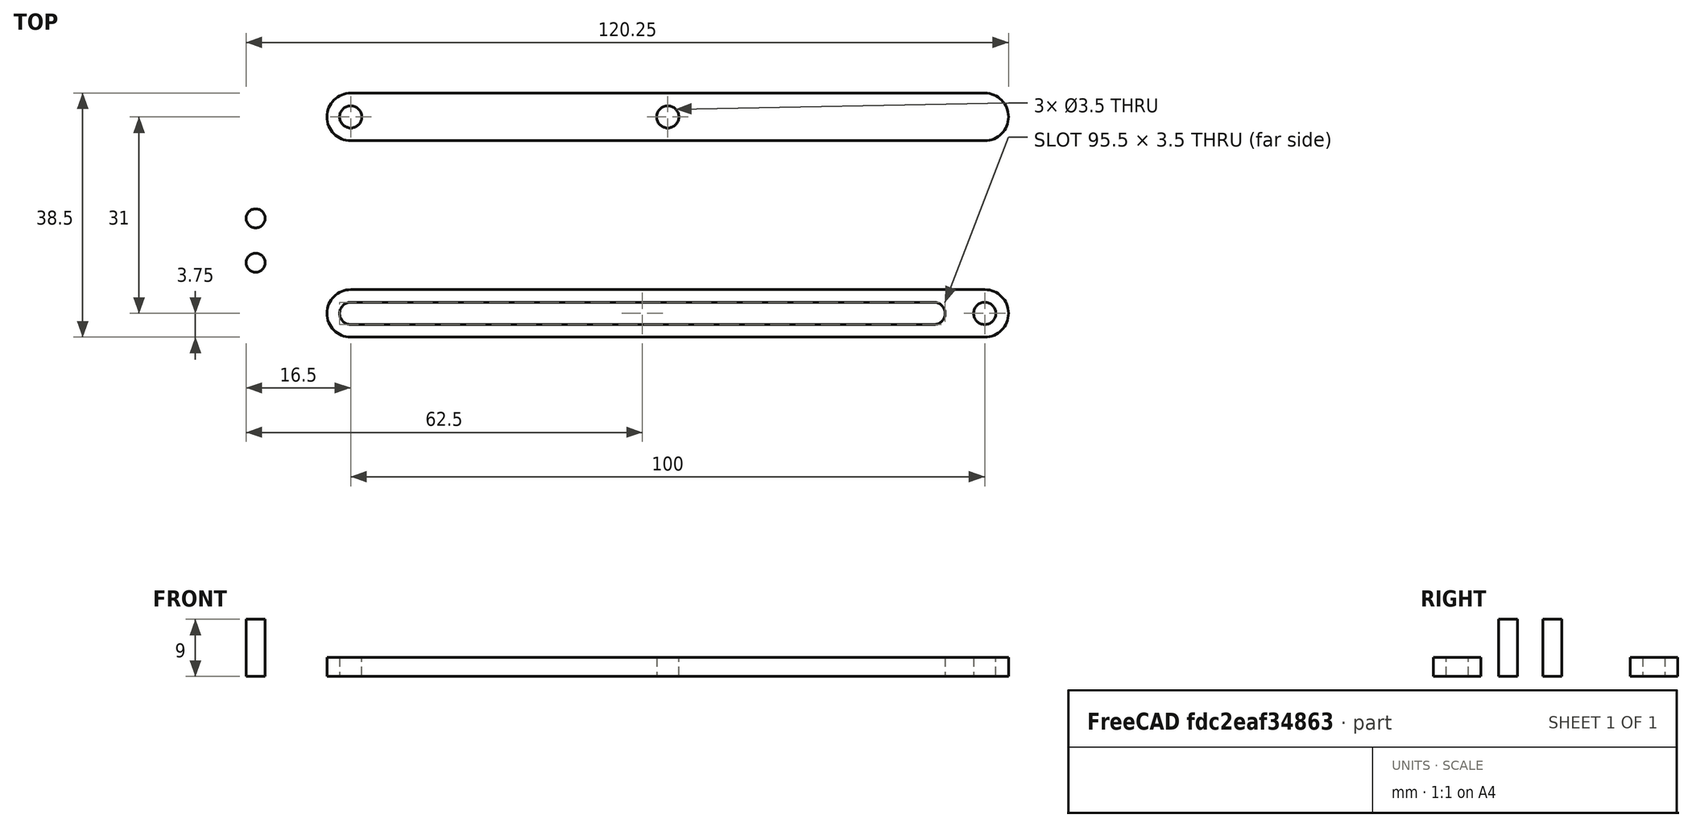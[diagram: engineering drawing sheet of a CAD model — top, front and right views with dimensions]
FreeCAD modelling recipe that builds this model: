
FCSTD DOCUMENT  (FreeCAD 1.0R39285 (Git))
Label: sissor_lift
License: All rights reserved
LicenseURL: https://en.wikipedia.org/wiki/All_rights_reserved
objects: PartDesign::Body×6, Sketcher::SketchObject×3, PartDesign::Pad×3, PartDesign::FeatureBase×3, PartDesign::SubShapeBinder×1, Assembly::JointGroup×1, Assembly::AssemblyObject×1
note: 28 computed .brp shape members not serialized (recipe doc carries the construction recipe); baked Part::Feature solids carry a one-line shape summary decoded from their .brp

FEATURE [Sketcher::SketchObject] Sketch
  ArcFitTolerance = 1e-06
  AttachmentSupport = -> [XY_Plane]
  FullyConstrained = true
  MakeInternals = false
  MapMode = 5
  sketch-geometry (9):
    g0: ArcOfCircle CenterX=-50 CenterY=2e-16 CenterZ=0 NormalX=0 NormalY=0 NormalZ=1 AngleXU=0 Radius=3.75 StartAngle=1.5708 EndAngle=4.71239
    g1: ArcOfCircle CenterX=50 CenterY=-2e-16 CenterZ=0 NormalX=0 NormalY=0 NormalZ=1 AngleXU=0 Radius=3.75 StartAngle=4.71239 EndAngle=7.85398
    g2: LineSegment StartX=-50 StartY=3.75 StartZ=0 EndX=50 EndY=3.75 EndZ=0
    g3: LineSegment StartX=-50 StartY=-3.75 StartZ=0 EndX=50 EndY=-3.75 EndZ=0
    g4: ArcOfCircle CenterX=-50 CenterY=2e-16 CenterZ=0 NormalX=0 NormalY=0 NormalZ=1 AngleXU=0 Radius=1.75 StartAngle=1.5708 EndAngle=4.71239
    g5: ArcOfCircle CenterX=42 CenterY=3e-16 CenterZ=0 NormalX=0 NormalY=0 NormalZ=1 AngleXU=0 Radius=1.75 StartAngle=4.71239 EndAngle=7.85398
    g6: LineSegment StartX=-50 StartY=1.75 StartZ=0 EndX=42 EndY=1.75 EndZ=0
    g7: LineSegment StartX=-50 StartY=-1.75 StartZ=0 EndX=42 EndY=-1.75 EndZ=0
    g8: Circle CenterX=50 CenterY=-2e-16 CenterZ=0 NormalX=0 NormalY=0 NormalZ=1 AngleXU=0 Radius=1.75
  constraints (20):
    c: Tangent(g0,g2) = 1.5708
    c: Tangent(g0,g3) = -1.5708
    c: Tangent(g1,g2) = 1.5708
    c: Tangent(g1,g3) = -1.5708
    c: Equal(g0,g1)
    c: Horizontal(g3)
    c: Symmetric(g0,g1,g-1)
    c: DistanceX(g0,g1) = 100
    c: DistanceY(g0,g0) = 7.5
    c: Tangent(g4,g6) = 1.5708
    c: Tangent(g4,g7) = -1.5708
    c: Tangent(g5,g6) = 1.5708
    c: Tangent(g5,g7) = -1.5708
    c: Equal(g4,g5)
    c: Horizontal(g7)
    c: Distance(g4,g4) = 3.5
    c: Coincident(g8,g1)
    c: Diameter(g8) = 3.5
    c: DistanceX(g5,g1) = 8
    c: Coincident(g4,g0)
FEATURE [PartDesign::Pad] Pad
  Direction = (0,0,1)
  Length = 3
  Length2 = 10
  Profile = -> Sketch
  ReferenceAxis = -> Sketch [N_Axis]
  Refine = true
  Suppressed = false
  Type = 0
FEATURE [PartDesign::Body] Body  label="base"
  AllowCompound = false
  Group = -> [Sketch,Pad]
  Origin = -> Origin
  Tip = -> Pad
FEATURE [PartDesign::SubShapeBinder] Binder
  BindCopyOnChange = 0
  BindMode = 0
  ClaimChildren = false
  Context = -> Body001 [Binder.]
  Fuse = false
  MakeFace = true
  OffsetFill = false
  OffsetIntersection = false
  OffsetJoinType = 0
  OffsetOpenResult = false
  PartialLoad = false
  Refine = true
  Relative = true
  Support = -> [Body]
  _Version = 2
FEATURE [Sketcher::SketchObject] Sketch001
  ArcFitTolerance = 1e-06
  AttachmentSupport = -> [XY_Plane001]
  ExternalGeometry = -> [Binder]
  FullyConstrained = true
  MakeInternals = false
  MapMode = 5
  sketch-geometry (6):
    g0: ArcOfCircle CenterX=-50 CenterY=1e-16 CenterZ=0 NormalX=0 NormalY=0 NormalZ=1 AngleXU=0 Radius=3.75 StartAngle=1.5708 EndAngle=4.71239
    g1: ArcOfCircle CenterX=50 CenterY=-1e-16 CenterZ=0 NormalX=0 NormalY=0 NormalZ=1 AngleXU=0 Radius=3.75 StartAngle=4.71239 EndAngle=7.85398
    g2: LineSegment StartX=-50 StartY=3.75 StartZ=0 EndX=50 EndY=3.75 EndZ=0
    g3: LineSegment StartX=-50 StartY=-3.75 StartZ=0 EndX=50 EndY=-3.75 EndZ=0
    g4: Circle CenterX=-50 CenterY=1e-16 CenterZ=0 NormalX=0 NormalY=0 NormalZ=1 AngleXU=0 Radius=1.75
    g5: Circle CenterX=0 CenterY=0 CenterZ=0 NormalX=0 NormalY=0 NormalZ=1 AngleXU=0 Radius=1.75
  constraints (13):
    c: Tangent(g0,g2) = 1.5708
    c: Tangent(g0,g3) = -1.5708
    c: Tangent(g1,g2) = 1.5708
    c: Tangent(g1,g3) = -1.5708
    c: Equal(g0,g1)
    c: Horizontal(g2)
    c: Symmetric(g0,g1,g-1)
    c: Equal(g2,g-3)
    c: Equal(g1,g-4)
    c: Coincident(g4,g0)
    c: Equal(g4,g-5)
    c: Coincident(g5,g-1)
    c: Equal(g5,g-5)
FEATURE [PartDesign::Pad] Pad001
  Direction = (0,0,1)
  Length = 3
  Length2 = 10
  Profile = -> Sketch001
  ReferenceAxis = -> Sketch001 [N_Axis]
  Refine = true
  Suppressed = false
  Type = 0
FEATURE [PartDesign::Body] Body001  label="arm_1"
  AllowCompound = false
  Group = -> [Binder,Sketch001,Pad001]
  Origin = -> Origin001
  Placement = pos=(0,14,0) rot=(0,0,1;0rad)
  Tip = -> Pad001
FEATURE [PartDesign::FeatureBase] Clone
  BaseFeature = -> Body001
  Placement = pos=(0,14,0) rot=(0,0,1;0rad)
  Suppressed = false
FEATURE [PartDesign::Body] Body002  label="arm_2"
  AllowCompound = false
  Group = -> [Clone]
  Origin = -> Origin002
  Placement = pos=(0,17,0) rot=(0,0,1;0rad)
  Tip = -> Clone
FEATURE [Sketcher::SketchObject] Sketch002
  ArcFitTolerance = 1e-06
  AttachmentSupport = -> [XY_Plane003]
  FullyConstrained = true
  MakeInternals = false
  MapMode = 5
  sketch-geometry (1):
    g0: Circle CenterX=0 CenterY=0 CenterZ=0 NormalX=0 NormalY=0 NormalZ=1 AngleXU=0 Radius=1.5
  constraints (2):
    c: Coincident(g0,g-1)
    c: Diameter(g0) = 3
FEATURE [PartDesign::Pad] Pad002
  Direction = (0,0,1)
  Length = 9
  Length2 = 10
  Profile = -> Sketch002
  ReferenceAxis = -> Sketch002 [N_Axis]
  Refine = true
  Suppressed = false
  Type = 0
FEATURE [PartDesign::Body] Body003  label="pin_1"
  AllowCompound = false
  Group = -> [Sketch002,Pad002]
  Origin = -> Origin003
  Placement = pos=(-65,0,0) rot=(0,0,1;0rad)
  Tip = -> Pad002
FEATURE [PartDesign::FeatureBase] Clone001
  BaseFeature = -> Body003
  Placement = pos=(-65,0,0) rot=(0,0,1;0rad)
  Suppressed = false
FEATURE [PartDesign::Body] Body004  label="pin_2"
  AllowCompound = false
  Group = -> [Clone001]
  Origin = -> Origin004
  Placement = pos=(0,8,0) rot=(0,0,1;0rad)
  Tip = -> Clone001
FEATURE [PartDesign::FeatureBase] Clone002
  BaseFeature = -> Body003
  Placement = pos=(-65,0,0) rot=(0,0,1;0rad)
  Suppressed = false
FEATURE [PartDesign::Body] Body005  label="pin_3"
  AllowCompound = false
  Group = -> [Clone002]
  Origin = -> Origin005
  Placement = pos=(0,15,0) rot=(0,0,1;0rad)
  Tip = -> Clone002
FEATURE [Assembly::JointGroup] Joints
FEATURE [Assembly::AssemblyObject] Assembly
  Group = -> [Joints,Body,Body001,Body002,Body003,Body004,Body005]
  Origin = -> Origin006
  Type = Assembly
